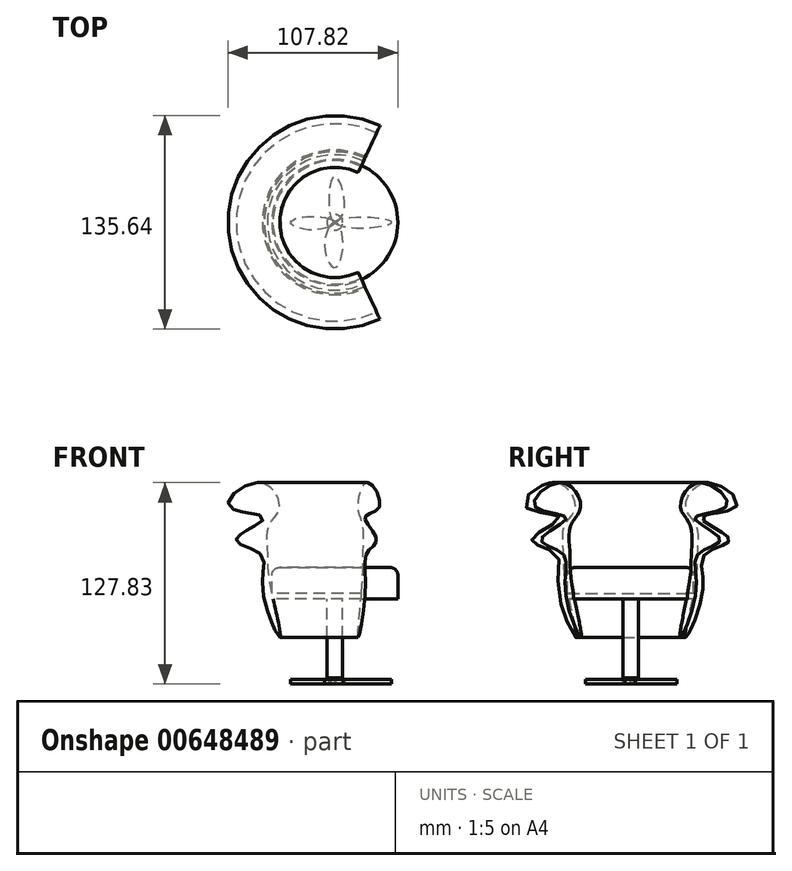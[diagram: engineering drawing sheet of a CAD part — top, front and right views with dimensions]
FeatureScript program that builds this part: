
annotation { "Feature Type Name" : "Feature", "Feature Type Description" : "" }
export const myFeature = defineFeature(function(context is Context, id is Id, definition is map)
    precondition{}
    {
        {
            var Q0;
            Q0=qCreatedBy(makeId("Top.planeOp"),FACE);
            var sketch = newSketch(context, id + "F0", { "sketchPlane" : qUnion([Q0])});
            skCircle(sketch, "E0", {"center": v(0, 0) * mm, "radius": 40 * mm});
            skSolve(sketch);
        }
        {
            var Q0;
            Q0=qCreatedBy(makeId("Front.planeOp"),FACE);
            var sketch = newSketch(context, id + "F1", { "sketchPlane" : qUnion([Q0])});
            skFitSpline(sketch, "E1", {"points": [v(-48.56, 53.82) * mm, v(-67.32, 39.01) * mm, v(-44.94, 31.44) * mm, v(-62.71, 17.94) * mm, v(-47.57, 8.72) * mm, v(-45.92, -13.66) * mm, v(-34.73, -44.6) * mm, v(-40.99, -11.36) * mm, v(-42.63, 10.37) * mm, v(-41.64, 27.16) * mm, v(-35.06, 38.35) * mm, v(-48.56, 53.82) * mm]});
            skSolve(sketch);
        }
        {
            var Q0;
            Q0=makeQuery(id+"F1.imprint","IMPRINT",FACE,{"disambiguationData":[TD([[makeQuery(id+"F1.imprint","IMPRINT",EDGE,{"derivedFrom":sQuery(id+"F1.wireOp",EDGE,"E1")}),1.0]])]});
            var Q1;
            Q1=sQuery(id+"F0.wireOp",EDGE,"E0");
            revolve(context, id + "F2", {"entities" : qUnion([Q0]), "axis" : qUnion([Q1]), "revolveType" : RevolveType.SYMMETRIC, "angle" : 230 * degree});
        }
        {
            var Q0;
            Q0 = qSketchRegion(id + "F0", true);
            extrude(context, id + "F3", {"entities" : qUnion([Q0]), "operationType" : NewBodyOperationType.ADD, "oppositeDirection" : true, "depth" : 20 * mm, "offsetDistance" : 25 * mm});
        }
        {
            var Q0;
            Q0=qCreatedBy(makeId("Top.planeOp"),FACE);
            cPlane(context, id + "F4", {"entities" : qUnion([Q0]), "cplaneType" : CPlaneType.OFFSET, "offset" : 20 * mm, "oppositeDirection" : true, "width" : 150 * mm, "height" : 150 * mm});
        }
        {
            var Q0;
            Q0=qCreatedBy(id+"F4.planeOp",FACE);
            var sketch = newSketch(context, id + "F5", { "sketchPlane" : qUnion([Q0])});
            skCircle(sketch, "E2", {"center": v(0, 0) * mm, "radius": 5 * mm});
            skSolve(sketch);
        }
        {
            var Q0;
            Q0 = qSketchRegion(id + "F5", true);
            extrude(context, id + "F6", {"entities" : qUnion([Q0]), "operationType" : NewBodyOperationType.ADD, "oppositeDirection" : true, "depth" : 50.2 * mm, "offsetDistance" : 25 * mm});
        }
        {
            var Q0;
            Q0=makeQuery(id+"F3.opExtrude","CAP_FACE",FACE,{"disambiguationData":[OSD([sQuery(id+"F0.wireOp",EDGE,"E0")])],"isStart":true});
            fillet(context, id + "F7", {"entities" : qUnion([Q0]), "radius" : 5 * mm, "tangentPropagation" : true, "allowEdgeOverflow" : false});
        }
        {
            var Q0;
            Q0=qCreatedBy(id+"F4.planeOp",FACE);
            cPlane(context, id + "F8", {"entities" : qUnion([Q0]), "cplaneType" : CPlaneType.OFFSET, "offset" : 51 * mm, "oppositeDirection" : true, "width" : 150 * mm, "height" : 150 * mm});
        }
        {
            var Q0;
            Q0=qCreatedBy(id+"F8.planeOp",FACE);
            var sketch = newSketch(context, id + "F9", { "sketchPlane" : qUnion([Q0])});
            skFitSpline(sketch, "E3", {"points": [v(0, 0) * mm, v(13.92, -3.52) * mm, v(36.06, 0) * mm, v(14.6, 3.19) * mm, v(0, 0) * mm]});
            skSolve(sketch);
        }
        {
            var Q0;
            Q0=qCreatedBy(id+"F8.planeOp",FACE);
            var sketch = newSketch(context, id + "F10", { "sketchPlane" : qUnion([Q0])});
            skFitSpline(sketch, "E4", {"points": [v(0, 0) * mm, v(-14.6, -4.86) * mm, v(-28.01, 0) * mm, v(-14.26, 3.86) * mm, v(0, 0) * mm]});
            skFitSpline(sketch, "E5", {"points": [v(0, 0) * mm, v(6.2, 10.23) * mm, v(0, 29.35) * mm, v(-3.86, 13.59) * mm, v(0, 0) * mm]});
            skFitSpline(sketch, "E6", {"points": [v(0, 0) * mm, v(-6.54, -13.92) * mm, v(0, -28.68) * mm, v(5.2, -13.25) * mm, v(0, 0) * mm]});
            skSolve(sketch);
        }
        {
            var Q0;
            {var subQ0=sQuery(id+"F10.wireOp",EDGE,"E5");var subQ1=sQuery(id+"F10.wireOp",EDGE,"E4");var subQ2=makeQuery(id+"F10.imprint","INTERSECT",VERTEX,{"derivedFrom":[subQ1,subQ0]});Q0=makeQuery(id+"F10.imprint","IMPRINT",FACE,{"disambiguationData":[TD([[makeQuery(id+"F10.imprint","IMPRINT",EDGE,{"disambiguationData":[TD([[subQ2,1.0]])],"derivedFrom":subQ0}),1.0]])]});}
            var Q1;
            {var subQ0=sQuery(id+"F10.wireOp",EDGE,"E6");var subQ1=sQuery(id+"F10.wireOp",EDGE,"E4");var subQ2=makeQuery(id+"F10.imprint","INTERSECT",VERTEX,{"derivedFrom":[subQ1,subQ0]});Q1=makeQuery(id+"F10.imprint","IMPRINT",FACE,{"disambiguationData":[TD([[makeQuery(id+"F10.imprint","IMPRINT",EDGE,{"disambiguationData":[TD([[subQ2,-1.0]])],"derivedFrom":subQ1}),-1.0]])]});}
            var Q2;
            {var subQ0=sQuery(id+"F10.wireOp",EDGE,"E6");var subQ1=sQuery(id+"F10.wireOp",EDGE,"E4");var subQ2=makeQuery(id+"F10.imprint","INTERSECT",VERTEX,{"derivedFrom":[subQ1,subQ0]});Q2=makeQuery(id+"F10.imprint","IMPRINT",FACE,{"disambiguationData":[TD([[makeQuery(id+"F10.imprint","IMPRINT",EDGE,{"disambiguationData":[TD([[subQ2,-1.0]])],"derivedFrom":subQ0}),1.0]])]});}
            extrude(context, id + "F11", {"entities" : qUnion([Q0, Q1, Q2]), "oppositeDirection" : true, "depth" : 3 * mm, "offsetDistance" : 25 * mm});
        }
        {
            var Q0;
            Q0 = qSketchRegion(id + "F9", true);
            extrude(context, id + "F12", {"entities" : qUnion([Q0]), "oppositeDirection" : true, "depth" : 3 * mm, "offsetDistance" : 25 * mm});
        }
    });
